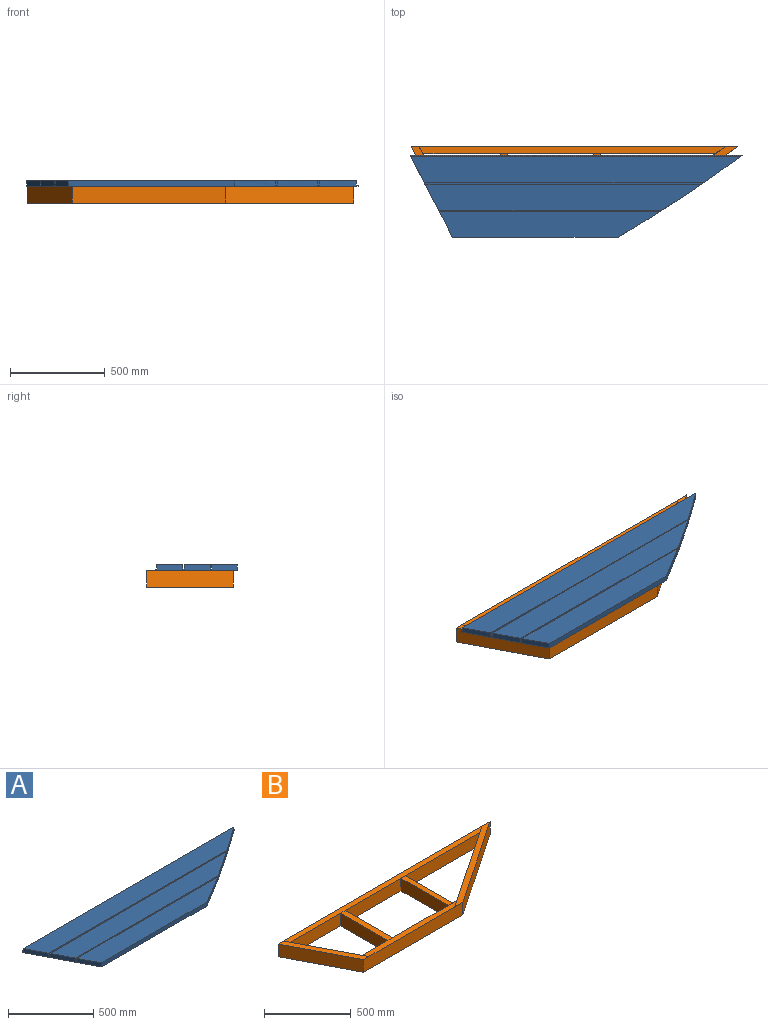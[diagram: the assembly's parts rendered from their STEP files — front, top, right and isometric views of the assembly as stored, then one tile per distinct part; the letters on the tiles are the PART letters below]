
ASSEMBLY  parts=2 mates=1
PART A: 16 faces, bbox 1753.8x431.8x29.4 mm
  f0: cylinder r=7233.9mm len=654.05mm, axis (0,0,-1), area 22278.7mm2, adj f2,f3,f4,f5,f6,f7,f8,f9
  f1: plane 431.8x224.37mm, normal (-0.89,-0.46,0), area 13814.1mm2, adj f2,f3,f4,f5,f6,f7,f8,f9
  f2: plane 1741.97x139.7mm, normal (0,0,1), area 224762.5mm2, adj f0,f1,f13,f15
  f3: plane 1460.99x139.7mm, normal (0,0,1), area 184449.2mm2, adj f0,f1,f10,f12
  f4: plane 1163.67x133.35mm, normal (0,0,1), area 136150.8mm2, adj f0,f1,f5,f9
  f5: plane 875.42x29.37mm, normal (0,-1,0), area 25710.1mm2, adj f0,f1,f4,f7
  f6: plane 1753.85x7.14mm, normal (0,1,0), area 12529.1mm2, adj f0,f1,f7,f14
  f7: plane 1753.85x431.8mm, normal (0,0,-1), area 573210.4mm2, adj f0,f1,f5,f6
  f8: plane 1176.98x6.35mm, normal (0,0,1), area 7431.6mm2, adj f0,f1,f9,f10
  f9: plane 1163.67x22.23mm, normal (0,1,0), area 25862.6mm2, adj f0,f1,f4,f8
  f10: plane 1176.98x22.23mm, normal (0,-1,0), area 26158.3mm2, adj f0,f1,f3,f8
  f11: plane 1473.53x6.35mm, normal (0,0,1), area 9317.1mm2, adj f0,f1,f12,f13
  f12: plane 1460.99x22.23mm, normal (0,1,0), area 32470.5mm2, adj f0,f1,f3,f11
  f13: plane 1473.53x22.23mm, normal (0,-1,0), area 32749.1mm2, adj f0,f1,f2,f11
  f14: plane 1753.85x6.35mm, normal (0,0,1), area 11099.2mm2, adj f0,f1,f6,f15
  f15: plane 1741.97x22.23mm, normal (0,1,0), area 38715.2mm2, adj f0,f1,f2,f14
PART B: 36 faces, bbox 1724.8x457.2x88.9 mm
  f0: plane 384.18x88.9mm, normal (-1,0,0), area 34153mm2, adj f7,f14,f15,f19,f26,f27,f28,f29
  f1: plane 384.18x88.9mm, normal (-1,0,0), area 34153mm2, adj f8,f14,f15,f19,f24,f25,f34,f35
  f2: plane 88.9x33.38mm, normal (0,1,0), area 2967.1mm2, adj f4,f6,f16,f19,f20,f21
  f3: plane 384.18x88.9mm, normal (1,0,0), area 34153mm2, adj f7,f14,f15,f19,f26,f27,f28,f29
  f4: plane 384.91x88.9mm, normal (1,0,0), area 34218mm2, adj f2,f6,f8,f14,f15,f19,f24,f25
  f5: plane 457.2x282.6mm, normal (0,0,1), area 20250.2mm2, adj f12,f13,f17,f18
  f6: plane 770.27x36.51mm, normal (0,0,1), area 26801.5mm2, adj f2,f4,f15,f18,f21,f23
  f7: plane 384.12x38.1mm, normal (0,0,1), area 14635.1mm2, adj f0,f3,f27,f28
  f8: plane 384.12x36.51mm, normal (0,0,1), area 14025.3mm2, adj f1,f4,f25,f35
  f9: plane 744.02x457.2mm, normal (0,0,1), area 29878.4mm2, adj f11,f12,f16,f18
  f10: plane 1615.79x36.51mm, normal (0,0,1), area 57658.7mm2, adj f12,f14,f31,f33
  f11: plane 678.67x457.2mm, normal (0.56,-0.83,0), area 72747.4mm2, adj f9,f12,f18,f19
  f12: plane 1724.77x88.9mm, normal (0,1,0), area 153331.7mm2, adj f5,f9,f10,f11,f13,f16,f17,f19
  f13: plane 457.2x237.57mm, normal (-0.89,-0.46,0), area 45804.7mm2, adj f5,f12,f18,f19
  f14: plane 1542.58x88.9mm, normal (0,-1,0), area 130691.5mm2, adj f0,f1,f3,f4,f10,f16,f17,f19
  f15: plane 736.97x88.9mm, normal (0,1,0), area 59073.2mm2, adj f0,f1,f3,f4,f6,f17,f19,f22
  f16: plane 678.67x457.2mm, normal (-0.56,0.83,0), area 61573mm2, adj f2,f9,f12,f14,f18,f19,f20,f32
  f17: plane 457.2x239.06mm, normal (0.89,0.46,0), area 38749.3mm2, adj f5,f12,f14,f15,f18,f19,f22,f30
  f18: plane 808.53x88.9mm, normal (0,-1,0), area 71878mm2, adj f5,f6,f9,f11,f13,f16,f17,f19
  f19: plane 1724.77x457.2mm, normal (0,0,-1), area 163258.4mm2, adj f0,f1,f2,f3,f4,f11,f12,f13
  f20: plane 53.16x35.78mm, normal (0,0,1), area 1.6mm2, adj f2,f16,f18,f21
  f21: plane 53.11x35.78mm, normal (0.56,-0.83,0), area 162.7mm2, adj f2,f6,f18,f20
  f22: plane 36.51x19.12mm, normal (0,0,1), area 1mm2, adj f15,f17,f18,f23
  f23: plane 36.51x19.09mm, normal (-0.89,-0.46,0), area 104.7mm2, adj f6,f15,f18,f22
  f24: plane 36.51x0.03mm, normal (0,0,1), area 0.9mm2, adj f1,f4,f15,f25
  f25: plane 36.51x2.54mm, normal (0,-1,0), area 92.7mm2, adj f1,f4,f8,f24
  f26: plane 38.1x0.03mm, normal (0,0,1), area 1mm2, adj f0,f3,f14,f27
  f27: plane 38.1x2.54mm, normal (0,1,0), area 96.8mm2, adj f0,f3,f7,f26
  f28: plane 38.1x2.54mm, normal (0,-1,0), area 96.8mm2, adj f0,f3,f7,f29
  f29: plane 38.1x0.03mm, normal (0,0,1), area 1mm2, adj f0,f3,f15,f28
  f30: plane 36.51x19.12mm, normal (0,0,1), area 1mm2, adj f12,f14,f17,f31
  f31: plane 36.51x19.09mm, normal (-0.89,-0.46,0), area 104.7mm2, adj f10,f12,f14,f30
  f32: plane 54.24x36.51mm, normal (0,0,1), area 1.7mm2, adj f12,f14,f16,f33
  f33: plane 54.2x36.51mm, normal (0.56,-0.83,0), area 166mm2, adj f10,f12,f14,f32
  f34: plane 36.51x0.03mm, normal (0,0,1), area 0.9mm2, adj f1,f4,f14,f35
  f35: plane 36.51x2.54mm, normal (0,1,0), area 92.7mm2, adj f1,f4,f8,f34
PLACE A t=(2609.62,3506.55,88.9)mm
PLACE B t=(6364.96,4327.03,0)mm
MATE fastened A.f7 <-> B.f5  axis (0,0,-1) through (-1505.92,-476.25,88.9)mm
